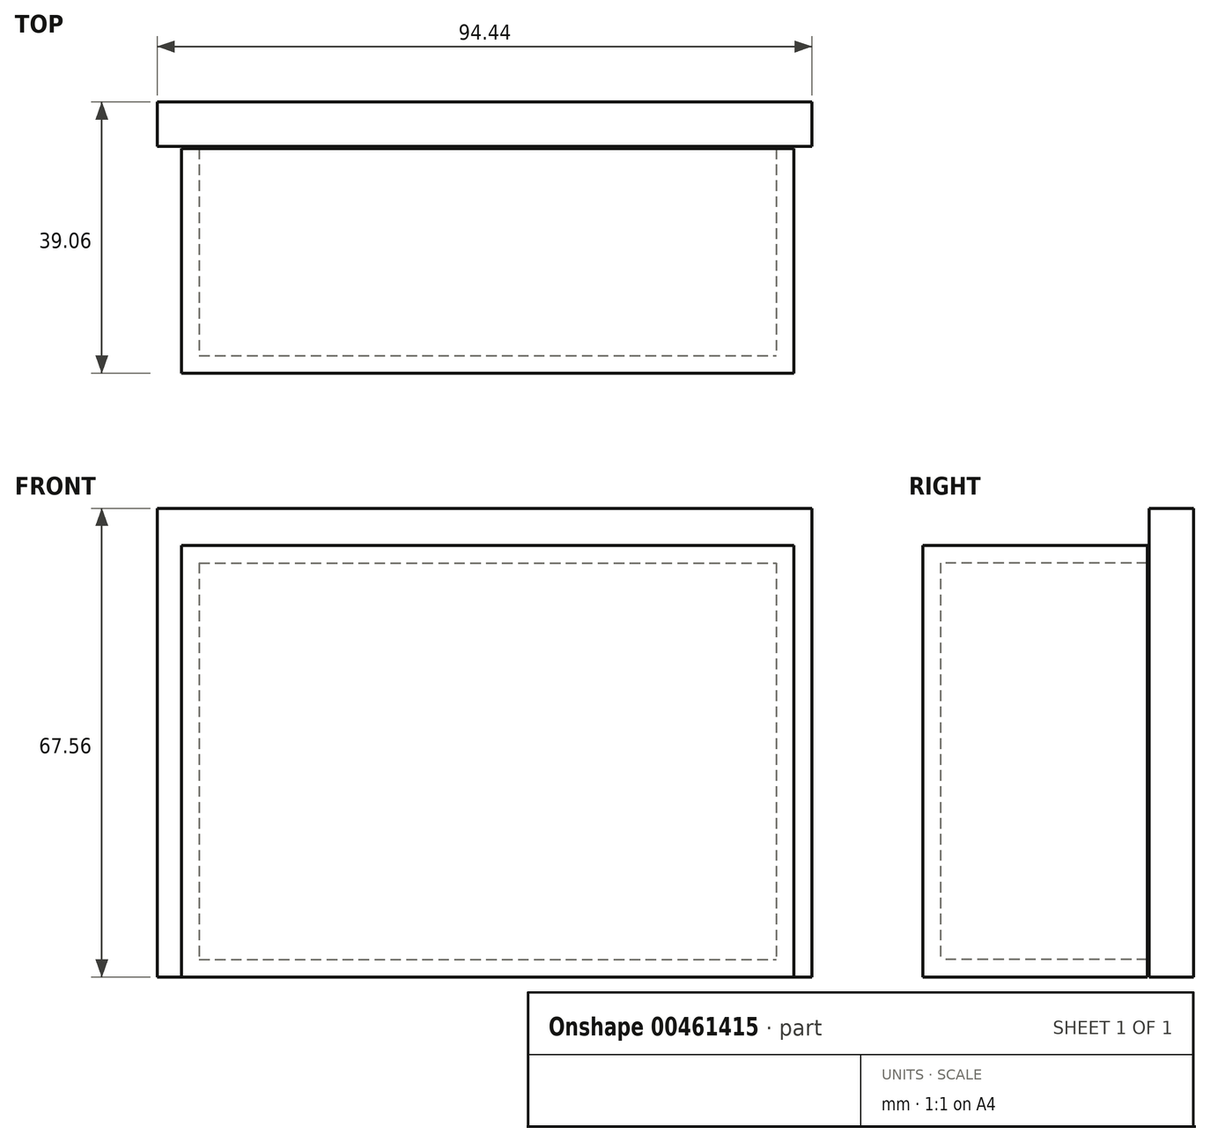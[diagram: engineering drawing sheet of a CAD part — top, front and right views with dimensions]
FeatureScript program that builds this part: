
annotation { "Feature Type Name" : "Feature", "Feature Type Description" : "" }
export const myFeature = defineFeature(function(context is Context, id is Id, definition is map)
    precondition{}
    {
        {
            var Q0;
            Q0=qCreatedBy(makeId("Top.planeOp"),FACE);
            var sketch = newSketch(context, id + "F0", { "sketchPlane" : qUnion([Q0])});
            skLineSegment(sketch, "E0.bottom", {"start": v(-41.1, 12.1) * mm, "end": v(47.22, 12.1) * mm});
            skLineSegment(sketch, "E0.top", {"start": v(-41.1, -20.26) * mm, "end": v(47.22, -20.26) * mm});
            skLineSegment(sketch, "E0.left", {"start": v(-41.1, 12.1) * mm, "end": v(-41.1, -20.26) * mm});
            skLineSegment(sketch, "E0.right", {"start": v(47.22, 12.1) * mm, "end": v(47.22, -20.26) * mm});
            skSolve(sketch);
        }
        {
            var Q0;
            Q0 = qSketchRegion(id + "F0", true);
            extrude(context, id + "F1", {"entities" : qUnion([Q0]), "depth" : 62.23 * mm});
        }
        {
            var Q0;
            Q0=makeQuery(id+"F1.opExtrude","SWEPT_FACE",FACE,{"disambiguationData":[OSD([sQuery(id+"F0.wireOp",EDGE,"E0.bottom")])]});
            shell(context, id + "F2", {"entities" : qUnion([Q0]), "thickness" : 2.54 * mm});
        }
        {
            var Q0;
            Q0=qCreatedBy(makeId("Top.planeOp"),FACE);
            var sketch = newSketch(context, id + "F3", { "sketchPlane" : qUnion([Q0])});
            skLineSegment(sketch, "E1.bottom", {"start": v(-44.6, 18.8) * mm, "end": v(49.84, 18.8) * mm});
            skLineSegment(sketch, "E1.top", {"start": v(-44.6, 12.39) * mm, "end": v(49.84, 12.39) * mm});
            skLineSegment(sketch, "E1.left", {"start": v(-44.6, 18.8) * mm, "end": v(-44.6, 12.39) * mm});
            skLineSegment(sketch, "E1.right", {"start": v(49.84, 18.8) * mm, "end": v(49.84, 12.39) * mm});
            skSolve(sketch);
        }
        {
            var Q0;
            Q0 = qSketchRegion(id + "F3", true);
            extrude(context, id + "F4", {"entities" : qUnion([Q0]), "depth" : 67.56 * mm});
        }
    });
